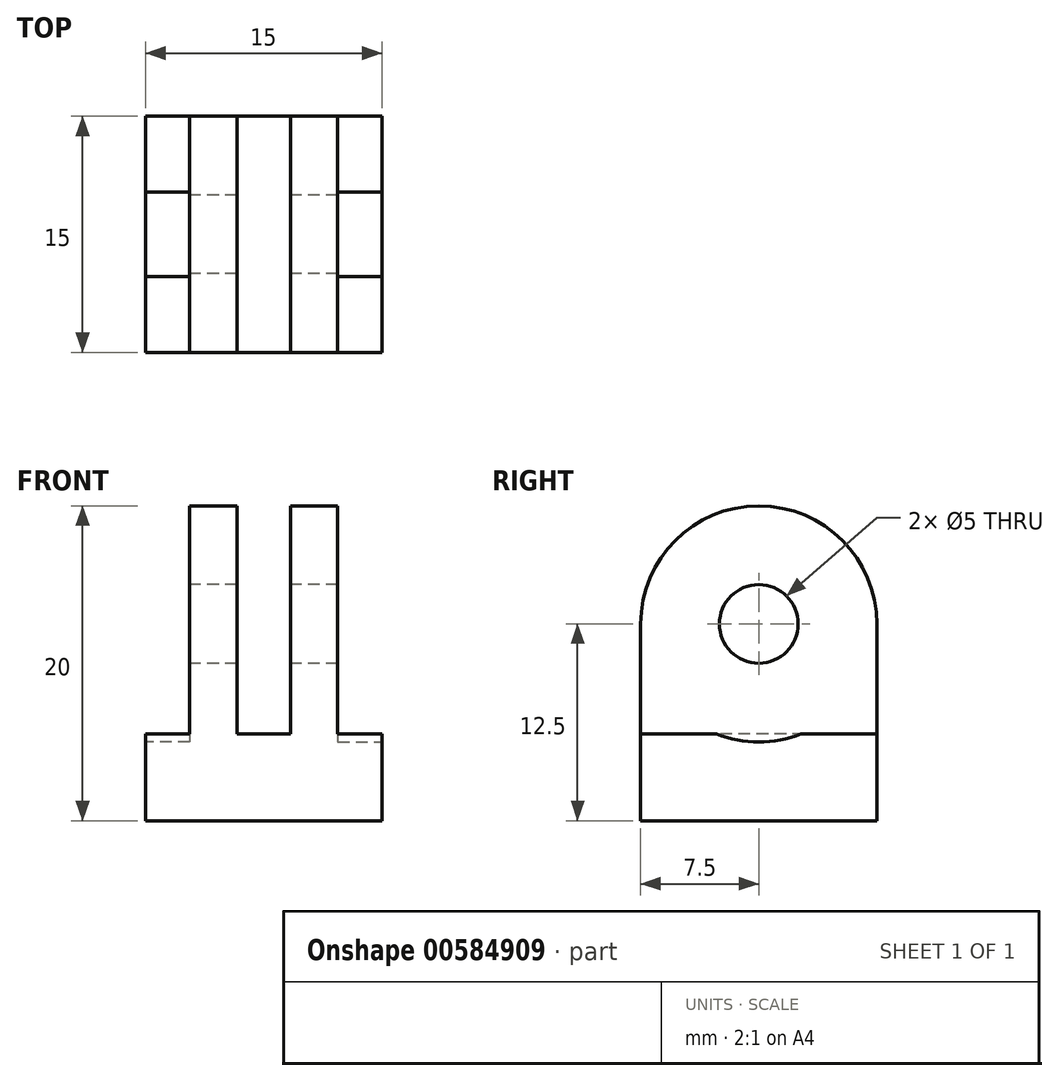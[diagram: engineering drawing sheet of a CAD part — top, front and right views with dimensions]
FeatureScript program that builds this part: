
annotation { "Feature Type Name" : "Feature", "Feature Type Description" : "" }
export const myFeature = defineFeature(function(context is Context, id is Id, definition is map)
    precondition{}
    {
        {
            var Q0;
            Q0=qCreatedBy(makeId("Right.planeOp"),FACE);
            var sketch = newSketch(context, id + "F0", { "sketchPlane" : qUnion([Q0])});
            skArc(sketch, "E0", {"start": v(7.5, 0) * mm, "mid": v(0, 7.5) * mm, "end": v(-7.5, 0) * mm});
            skCircle(sketch, "E1", {"center": v(0, 0) * mm, "radius": 2.5 * mm});
            skLineSegment(sketch, "E2", {"start": v(-7.5, 0) * mm, "end": v(-7.5, -12.5) * mm});
            skLineSegment(sketch, "E3", {"start": v(7.5, 0) * mm, "end": v(7.5, -12.5) * mm});
            skLineSegment(sketch, "E4", {"start": v(7.5, -12.5) * mm, "end": v(-7.5, -12.5) * mm});
            skSolve(sketch);
        }
        {
            var Q0;
            Q0=makeQuery(id+"F0.imprint","IMPRINT",FACE,{"disambiguationData":[TD([[makeQuery(id+"F0.imprint","IMPRINT",EDGE,{"derivedFrom":sQuery(id+"F0.wireOp",EDGE,"E0")}),1.0]])]});
            extrude(context, id + "F1", {"entities" : qUnion([Q0]), "endBound" : BoundingType.SYMMETRIC, "depth" : 15 * mm});
        }
        {
            var Q0;
            Q0=qCreatedBy(makeId("Front.planeOp"),FACE);
            var sketch = newSketch(context, id + "F2", { "sketchPlane" : qUnion([Q0])});
            skLineSegment(sketch, "E5", {"start": v(0, -18.95) * mm, "end": v(0, 19.26) * mm, "construction": true});
            skLineSegment(sketch, "E6", {"start": v(-12.45, 0) * mm, "end": v(16.05, 0) * mm, "construction": true});
            skLineSegment(sketch, "E7.0", {"start": v(-1.7, -7) * mm, "end": v(-1.7, 8.45) * mm});
            skLineSegment(sketch, "E8.0.MirrorCS", {"start": v(1.7, -7) * mm, "end": v(1.7, 8.45) * mm});
            skLineSegment(sketch, "E9.0", {"start": v(-8.58, -7) * mm, "end": v(-4.7, -7) * mm});
            skLineSegment(sketch, "E10.0", {"start": v(4.7, -7) * mm, "end": v(4.7, 8.45) * mm});
            skLineSegment(sketch, "E11.0", {"start": v(-4.7, -7) * mm, "end": v(-4.7, 8.45) * mm});
            skPoint(sketch, "E12.orphan", {"position": v(-1.7, -18.95) * mm});
            skLineSegment(sketch, "E13.trimOffspring", {"start": v(4.7, -7) * mm, "end": v(8.53, -7) * mm});
            skPoint(sketch, "E14.orphan", {"position": v(1.7, -18.95) * mm});
            skLineSegment(sketch, "E15", {"start": v(-8.58, 8.45) * mm, "end": v(-4.7, 8.45) * mm});
            skLineSegment(sketch, "E16", {"start": v(8.53, 8.45) * mm, "end": v(8.53, -7) * mm});
            skLineSegment(sketch, "E17", {"start": v(-8.58, -7) * mm, "end": v(-8.58, 8.45) * mm});
            skLineSegment(sketch, "E18.trimOffspring", {"start": v(-1.7, 8.45) * mm, "end": v(1.7, 8.45) * mm});
            skPoint(sketch, "E19.orphan", {"position": v(-1.7, 19.26) * mm});
            skPoint(sketch, "E20.orphan", {"position": v(1.7, 19.26) * mm});
            skLineSegment(sketch, "E21.trimOffspring", {"start": v(4.7, 8.45) * mm, "end": v(8.53, 8.45) * mm});
            skLineSegment(sketch, "E22", {"start": v(1.7, -7) * mm, "end": v(-1.7, -7) * mm});
            skSolve(sketch);
        }
        {
            var Q0;
            {Q0=qUnion([makeQuery(id+"F2.imprint","IMPRINT",FACE,{"disambiguationData":[TD([[makeQuery(id+"F2.imprint","IMPRINT",EDGE,{"derivedFrom":sQuery(id+"F2.wireOp",EDGE,"E7.0")}),-1.0]])]}),makeQuery(id+"F2.imprint","IMPRINT",FACE,{"disambiguationData":[TD([[makeQuery(id+"F2.imprint","IMPRINT",EDGE,{"derivedFrom":sQuery(id+"F2.wireOp",EDGE,"E9.0")}),1.0]])]}),makeQuery(id+"F2.imprint","IMPRINT",FACE,{"disambiguationData":[TD([[makeQuery(id+"F2.imprint","IMPRINT",EDGE,{"derivedFrom":sQuery(id+"F2.wireOp",EDGE,"E10.0")}),-1.0]])]})]);}
            extrude(context, id + "F3", {"entities" : qUnion([Q0]), "operationType" : NewBodyOperationType.REMOVE, "endBound" : BoundingType.SYMMETRIC, "oppositeDirection" : true, "depth" : 32.83 * mm});
        }
        {
            var Q0;
            Q0=makeQuery(id+"F1.opExtrude","CAP_FACE",FACE,{"disambiguationData":[OSD([sQuery(id+"F0.wireOp",EDGE,"E0"),sQuery(id+"F0.wireOp",EDGE,"E1"),sQuery(id+"F0.wireOp",EDGE,"E2"),sQuery(id+"F0.wireOp",EDGE,"E3"),sQuery(id+"F0.wireOp",EDGE,"E4")])],"isStart":true});
            var sketch = newSketch(context, id + "F4", { "sketchPlane" : qUnion([Q0])});
            skCircle(sketch, "E23", {"center": v(0, 0) * mm, "radius": 7.5 * mm});
            skSolve(sketch);
        }
        {
            var Q0;
            {var subQ0=makeQuery(id+"F3.boolean.opBoolean","INTERSECT",EDGE,{"derivedFrom":[makeQuery(id+"F1.opExtrude","CAP_FACE",FACE,{"disambiguationData":[OSD([sQuery(id+"F0.wireOp",EDGE,"E0"),sQuery(id+"F0.wireOp",EDGE,"E1"),sQuery(id+"F0.wireOp",EDGE,"E2"),sQuery(id+"F0.wireOp",EDGE,"E3"),sQuery(id+"F0.wireOp",EDGE,"E4")])],"isStart":true}),makeQuery(id+"F3.opExtrude","SWEPT_FACE",FACE,{"disambiguationData":[OSD([sQuery(id+"F2.wireOp",EDGE,"E9.0")])]})]});var subQ1=sQuery(id+"F4.wireOp",EDGE,"E23");var subQ3=makeQuery(id+"F4.imprint","INTERSECT",VERTEX,{"disambiguationData":[OD(0.0)],"derivedFrom":[subQ0,subQ1]});Q0=qUnion([makeQuery(id+"F4.imprint","IMPRINT",FACE,{"disambiguationData":[TD([[makeQuery(id+"F4.imprint","IMPRINT",EDGE,{"disambiguationData":[TD([[subQ3,-1.0]])],"derivedFrom":subQ1}),1.0]])]}),makeQuery(id+"F4.imprint","IMPRINT",FACE,{"disambiguationData":[TD([[makeQuery(id+"F4.imprint","IMPRINT",EDGE,{"disambiguationData":[TD([[subQ3,1.0]])],"derivedFrom":subQ1}),1.0]])]})]);}
            var Q1;
            Q1=makeQuery(id+"F3.boolean.opBoolean","COPY",FACE,{"derivedFrom":makeQuery(id+"F3.opExtrude","SWEPT_FACE",FACE,{"disambiguationData":[OSD([sQuery(id+"F2.wireOp",EDGE,"E11.0")])]})});
            extrude(context, id + "F5", {"entities" : qUnion([Q0]), "operationType" : NewBodyOperationType.REMOVE, "endBound" : BoundingType.UP_TO_SURFACE, "oppositeDirection" : true, "endBoundEntityFace" : qUnion([Q1]), "depth" : 25 * mm});
        }
        {
            var Q0;
            Q0=makeQuery(id+"F1.opExtrude","CAP_FACE",FACE,{"disambiguationData":[OSD([sQuery(id+"F0.wireOp",EDGE,"E0"),sQuery(id+"F0.wireOp",EDGE,"E1"),sQuery(id+"F0.wireOp",EDGE,"E2"),sQuery(id+"F0.wireOp",EDGE,"E3"),sQuery(id+"F0.wireOp",EDGE,"E4")])],"isStart":false});
            var sketch = newSketch(context, id + "F6", { "sketchPlane" : qUnion([Q0])});
            skCircle(sketch, "E24", {"center": v(0, 0) * mm, "radius": 7.5 * mm});
            skSolve(sketch);
        }
        {
            var Q0;
            {var subQ0=makeQuery(id+"F3.boolean.opBoolean","INTERSECT",EDGE,{"derivedFrom":[makeQuery(id+"F1.opExtrude","CAP_FACE",FACE,{"disambiguationData":[OSD([sQuery(id+"F0.wireOp",EDGE,"E0"),sQuery(id+"F0.wireOp",EDGE,"E1"),sQuery(id+"F0.wireOp",EDGE,"E2"),sQuery(id+"F0.wireOp",EDGE,"E3"),sQuery(id+"F0.wireOp",EDGE,"E4")])],"isStart":false}),makeQuery(id+"F3.opExtrude","SWEPT_FACE",FACE,{"disambiguationData":[OSD([sQuery(id+"F2.wireOp",EDGE,"E13.trimOffspring")])]})]});var subQ1=sQuery(id+"F6.wireOp",EDGE,"E24");var subQ3=makeQuery(id+"F6.imprint","INTERSECT",VERTEX,{"disambiguationData":[OD(0.0)],"derivedFrom":[subQ0,subQ1]});Q0=qUnion([makeQuery(id+"F6.imprint","IMPRINT",FACE,{"disambiguationData":[TD([[makeQuery(id+"F6.imprint","IMPRINT",EDGE,{"disambiguationData":[TD([[subQ3,1.0]])],"derivedFrom":subQ1}),1.0]])]}),makeQuery(id+"F6.imprint","IMPRINT",FACE,{"disambiguationData":[TD([[makeQuery(id+"F6.imprint","IMPRINT",EDGE,{"disambiguationData":[TD([[subQ3,-1.0]])],"derivedFrom":subQ1}),1.0]])]})]);}
            var Q1;
            Q1=makeQuery(id+"F3.boolean.opBoolean","COPY",FACE,{"derivedFrom":makeQuery(id+"F3.opExtrude","SWEPT_FACE",FACE,{"disambiguationData":[OSD([sQuery(id+"F2.wireOp",EDGE,"E10.0")])]})});
            extrude(context, id + "F7", {"entities" : qUnion([Q0]), "operationType" : NewBodyOperationType.REMOVE, "endBound" : BoundingType.UP_TO_SURFACE, "oppositeDirection" : true, "endBoundEntityFace" : qUnion([Q1]), "depth" : 25 * mm});
        }
    });
